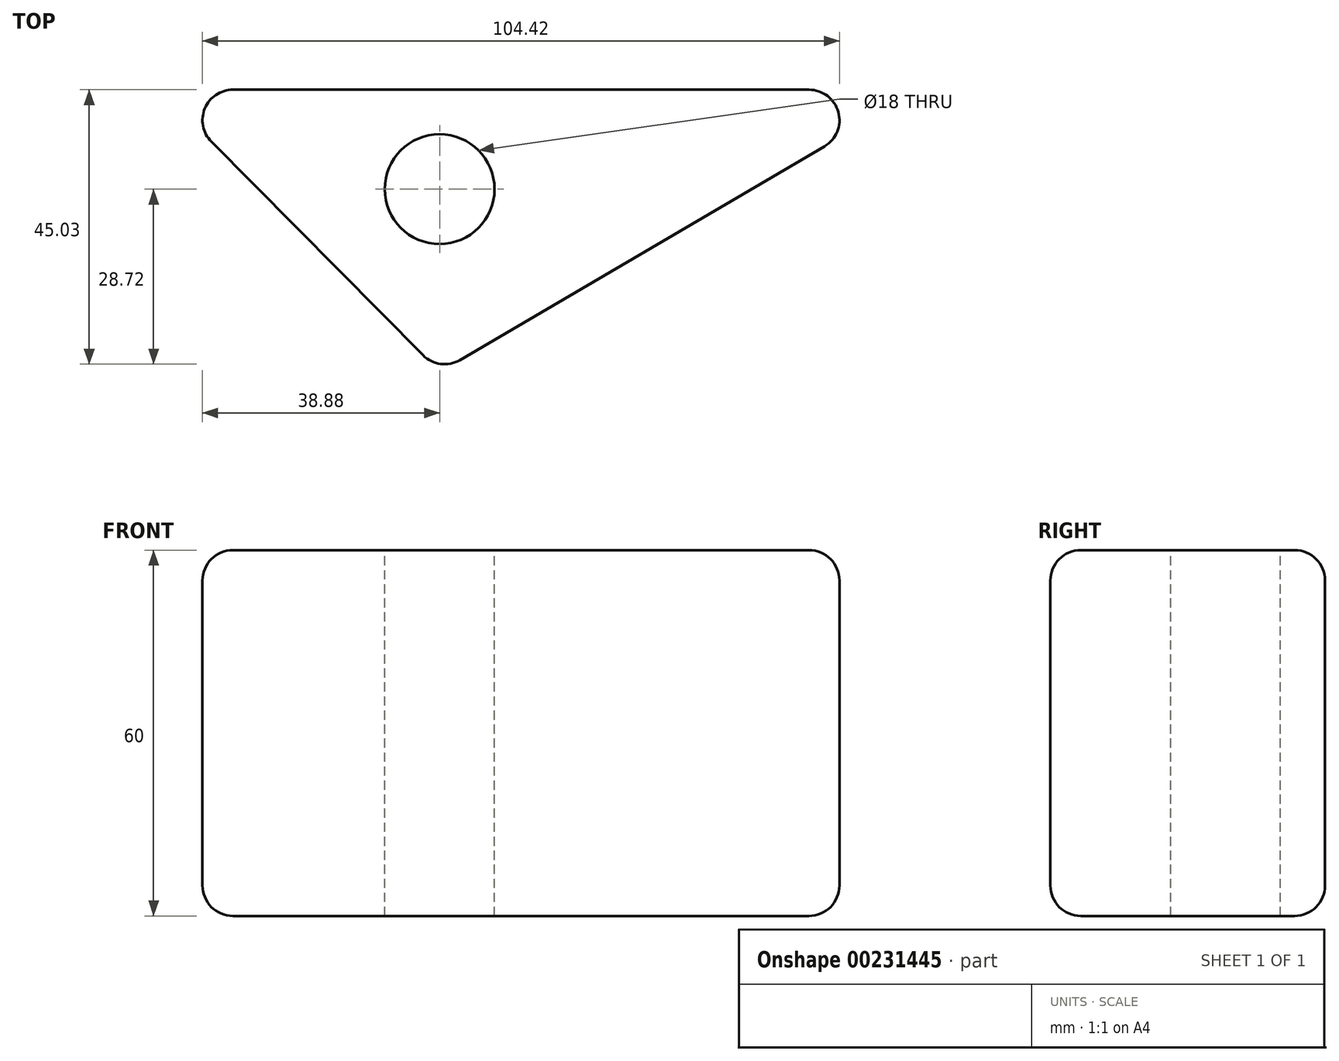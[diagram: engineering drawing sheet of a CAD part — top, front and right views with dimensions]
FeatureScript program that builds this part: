
annotation { "Feature Type Name" : "Feature", "Feature Type Description" : "" }
export const myFeature = defineFeature(function(context is Context, id is Id, definition is map)
    precondition{}
    {
        {
            var Q0;
            Q0=qCreatedBy(makeId("Top.planeOp"),FACE);
            var sketch = newSketch(context, id + "F0", { "sketchPlane" : qUnion([Q0])});
            skLineSegment(sketch, "E0", {"start": v(0, 0) * mm, "end": v(-45.87, 46.3) * mm});
            skLineSegment(sketch, "E1", {"start": v(-45.87, 46.3) * mm, "end": v(78.94, 46.3) * mm});
            skLineSegment(sketch, "E2", {"start": v(78.94, 46.3) * mm, "end": v(0, 0) * mm});
            skSolve(sketch);
        }
        {
            var Q0;
            Q0 = qSketchRegion(id + "F0", true);
            extrude(context, id + "F1", {"entities" : qUnion([Q0]), "depth" : 60 * mm});
        }
        {
            var Q0;
            Q0=makeQuery(id+"F1.opExtrude","CAP_FACE",FACE,{"disambiguationData":[OSD([sQuery(id+"F0.wireOp",EDGE,"E0"),sQuery(id+"F0.wireOp",EDGE,"E1"),sQuery(id+"F0.wireOp",EDGE,"E2")])],"isStart":false});
            var sketch = newSketch(context, id + "F2", { "sketchPlane" : qUnion([Q0])});
            skCircle(sketch, "E3", {"center": v(0, 30) * mm, "radius": 9 * mm});
            skSolve(sketch);
        }
        {
            var Q0;
            Q0 = qSketchRegion(id + "F2", true);
            extrude(context, id + "F3", {"entities" : qUnion([Q0]), "operationType" : NewBodyOperationType.REMOVE, "endBound" : BoundingType.THROUGH_ALL, "oppositeDirection" : true, "depth" : 25 * mm});
        }
        {
            var Q0;
            Q0=makeQuery(id+"F1.opExtrude","SWEPT_EDGE",EDGE,{"disambiguationData":[OSD([sQuery(id+"F0.wireOp",EDGE,"E0"),sQuery(id+"F0.wireOp",EDGE,"E1")])]});
            var Q1;
            Q1=makeQuery(id+"F1.opExtrude","SWEPT_EDGE",EDGE,{"disambiguationData":[OSD([sQuery(id+"F0.wireOp",EDGE,"E0"),sQuery(id+"F0.wireOp",EDGE,"E2")])]});
            var Q2;
            Q2=makeQuery(id+"F1.opExtrude","SWEPT_EDGE",EDGE,{"disambiguationData":[OSD([sQuery(id+"F0.wireOp",EDGE,"E1"),sQuery(id+"F0.wireOp",EDGE,"E2")])]});
            fillet(context, id + "F4", {"entities" : qUnion([Q0, Q1, Q2]), "radius" : 5 * mm, "tangentPropagation" : true, "allowEdgeOverflow" : false});
        }
        {
            var Q0;
            Q0=makeQuery(id+"F1.opExtrude","CAP_EDGE",EDGE,{"disambiguationData":[OSD([sQuery(id+"F0.wireOp",EDGE,"E2")])],"isStart":true});
            var Q1;
            Q1=makeQuery(id+"F1.opExtrude","CAP_EDGE",EDGE,{"disambiguationData":[OSD([sQuery(id+"F0.wireOp",EDGE,"E2")])],"isStart":false});
            fillet(context, id + "F5", {"entities" : qUnion([Q0, Q1]), "radius" : 5 * mm, "tangentPropagation" : true, "allowEdgeOverflow" : false});
        }
    });
